# Revit family: Domotics-SerieCivili-GEWISS-27COMBIIN_SYSTEM-IP65_CALOTTA_2M
name_source: partatom
category: Apparecchi elettrici
revit_build: Autodesk Revit 2016 (Build: 20161004_0715(x64)
units: mm (PartAtom-declared; Revit-internal decimal feet)

## family parameters
Basato su piano di lavoro = No
Condiviso = No
Mantenere orientamento annotazione = No
Numero OmniClass = 23.80.30.14.24
Punto di calcolo locali = No
Quota connettore circolare = Usa diametro
Sempre verticale = Sì
Taglio con vuoti quando caricato = No
Tipo di parte = Normale
Titolo OmniClass = Junction Boxes

## types (1)
- GW27403 - Calotta stagna portella rigida 2 posti IP65
    Altezza da terra = 850 mm  [stored 2.78871 ft]
    Catalogo = DOMOTICS
    Catalogo Serie = 27COMBI
    Classe isolamento = II
    Codice EAN = 8011564789913
    Codice Electrocod = 0220
    Colore = Grigio RAL 7035
    Colore portella = Trasparente fume'
    Coppia serraggio viti = 0,8NM
    Descrizione = CALOTTA STAGNA PORT. RIGIDA 2 POSTI IP65
    Dimensioni BxH (mm) = 75x85
    Finitura = <Per categoria>
    Glow Wire Test = 650°C
    Grado di protezione = IP65
    IDF = 1318ab41-dd95-4df6-a8de-c85cd3ac870c
    IDT = 428b0478-5cd0-4e39-b324-3b7b05b338cb
    Immagine tipo = GW27403.jpg
    Larghezza = 75 mm
    Lunghezza = 85 mm  [stored 0.278871 ft]
    Modello = GW27403
    N. moduli SYSTEM = 2
    Norma di riferimento = EN 60669-1
    Norma di riferimento: = EN 60669-1
    Produttore = GEWISS S.p.A.
    Profondità = 20 mm  [stored 0.0656168 ft]
    Resistenza agli urti = IK09
    SEO = Calotta
    Scheda Tecnica = https://www.gewiss.com
    Temperatura di installazione = -25 +60 °C
    Termopressione con biglia = 70 °C
    Tipo portella = Rigida IK09
    URL = https://www.gewiss.com
    Versione file RFA = 19.4
    Vetro Sportello = Vetro
    Viti coperchio = Acciaio inox

note: [stored X ft] marks values corroborated as IEEE doubles in the binary element streams (Revit-internal decimal feet)
